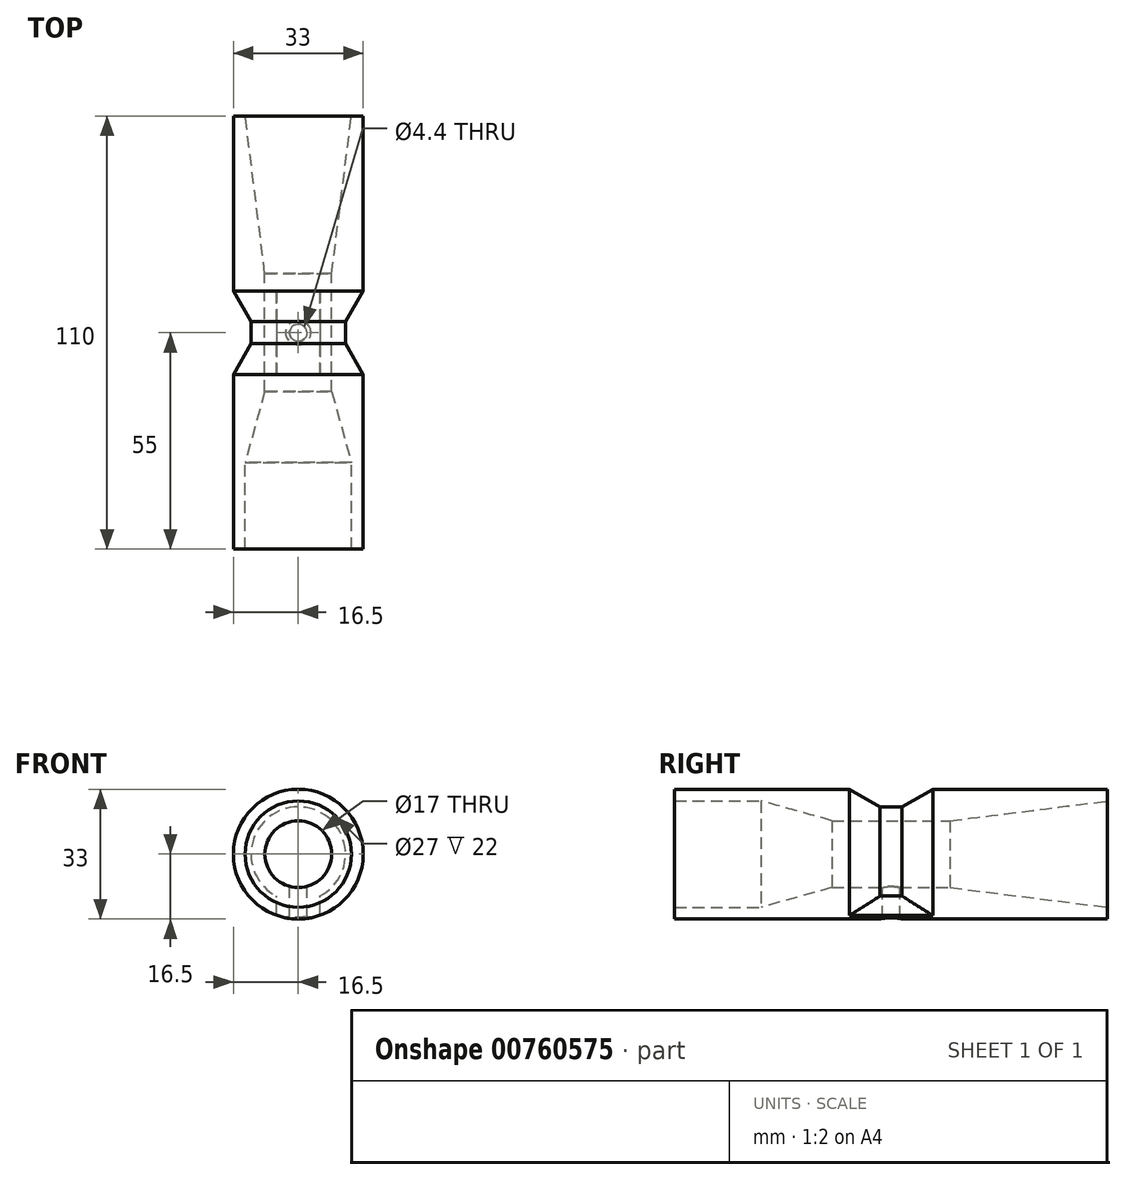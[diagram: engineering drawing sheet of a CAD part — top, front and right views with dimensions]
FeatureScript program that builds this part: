
annotation { "Feature Type Name" : "Feature", "Feature Type Description" : "" }
export const myFeature = defineFeature(function(context is Context, id is Id, definition is map)
    precondition{}
    {
        {
            var Q0;
            Q0=qCreatedBy(makeId("Front.planeOp"),FACE);
            var sketch = newSketch(context, id + "F0", { "sketchPlane" : qUnion([Q0])});
            skCircle(sketch, "E0", {"center": v(0, 0) * mm, "radius": 13.5 * mm});
            skCircle(sketch, "E1", {"center": v(0, 0) * mm, "radius": 16.5 * mm});
            skCircle(sketch, "E2", {"center": v(0, 0) * mm, "radius": 23.5 * mm});
            skCircle(sketch, "E3", {"center": v(0, 0) * mm, "radius": 26.5 * mm});
            skSolve(sketch);
        }
        {
            var Q0;
            Q0=qCreatedBy(makeId("Right.planeOp"),FACE);
            var sketch = newSketch(context, id + "F1", { "sketchPlane" : qUnion([Q0])});
            skLineSegment(sketch, "E4", {"start": v(0, 0) * mm, "end": v(0, 57.21) * mm, "construction": true});
            skLineSegment(sketch, "E5", {"start": v(15, 32.18) * mm, "end": v(15, -25.03) * mm, "construction": true});
            skLineSegment(sketch, "E6", {"start": v(55, 32.18) * mm, "end": v(55, -25.03) * mm, "construction": true});
            skLineSegment(sketch, "E7", {"start": v(55, 13.5) * mm, "end": v(-55, 13.5) * mm});
            skLineSegment(sketch, "E8", {"start": v(-15, 31.27) * mm, "end": v(-15, -25.94) * mm, "construction": true});
            skLineSegment(sketch, "E9", {"start": v(-55, 31.87) * mm, "end": v(-55, -25.34) * mm, "construction": true});
            skPoint(sketch, "E10", {"position": v(-33, 13.5) * mm});
            skLineSegment(sketch, "E11", {"start": v(-15, 8.5) * mm, "end": v(15, 8.5) * mm});
            skLineSegment(sketch, "E12", {"start": v(-15, 8.5) * mm, "end": v(-33, 13.5) * mm});
            skLineSegment(sketch, "E13", {"start": v(15, 8.5) * mm, "end": v(55, 13.5) * mm});
            skLineSegment(sketch, "E14", {"start": v(-32.07, 13.24) * mm, "end": v(-32.07, 0) * mm});
            skLineSegment(sketch, "E15", {"start": v(-32.07, 0) * mm, "end": v(48.4, 0) * mm});
            skLineSegment(sketch, "E16", {"start": v(48.4, 0) * mm, "end": v(48.4, 12.68) * mm});
            skLineSegment(sketch, "E17.MirrorCS", {"start": v(-15, -8.5) * mm, "end": v(15, -8.5) * mm, "construction": true});
            skLineSegment(sketch, "E18.MirrorCS", {"start": v(55, -13.5) * mm, "end": v(-55, -13.5) * mm, "construction": true});
            skLineSegment(sketch, "E19.bottom", {"start": v(10.63, -16.5) * mm, "end": v(-10.62, -16.5) * mm});
            skLineSegment(sketch, "E19.top", {"start": v(10.63, -7.75) * mm, "end": v(-10.62, -7.75) * mm});
            skLineSegment(sketch, "E19.left", {"start": v(10.63, -16.5) * mm, "end": v(10.63, -7.75) * mm});
            skLineSegment(sketch, "E19.right", {"start": v(-10.62, -16.5) * mm, "end": v(-10.62, -7.75) * mm});
            skPoint(sketch, "E19.middle", {"position": v(0, -12.13) * mm});
            skLineSegment(sketch, "E20", {"start": v(0, 0) * mm, "end": v(0, -13.5) * mm, "construction": true});
            skSolve(sketch);
        }
        {
            var Q0;
            Q0=makeQuery(id+"F0.imprint","IMPRINT",FACE,{"disambiguationData":[TD([[makeQuery(id+"F0.imprint","IMPRINT",EDGE,{"derivedFrom":sQuery(id+"F0.wireOp",EDGE,"E0")}),-1.0]])]});
            var Q1;
            Q1=sQuery(id+"F1.wireOp",VERTEX,"E7.end");
            extrude(context, id + "F2", {"entities" : qUnion([Q0]), "endBound" : BoundingType.UP_TO_VERTEX, "depth" : 60 * mm, "endBoundEntityVertex" : qUnion([Q1]), "offsetDistance" : 25 * mm});
        }
        {
            var Q0;
            Q0=makeQuery(id+"F2.opExtrude","CAP_FACE",FACE,{"disambiguationData":[OSD([sQuery(id+"F0.wireOp",EDGE,"E0"),sQuery(id+"F0.wireOp",EDGE,"E1")])],"isStart":true});
            var Q1;
            Q1=sQuery(id+"F1.wireOp",VERTEX,"E7.start");
            extrude(context, id + "F3", {"entities" : qUnion([Q0]), "operationType" : NewBodyOperationType.ADD, "endBound" : BoundingType.UP_TO_VERTEX, "depth" : 25 * mm, "endBoundEntityVertex" : qUnion([Q1]), "offsetDistance" : 25 * mm});
        }
        {
            var Q0;
            Q0=makeQuery(id+"F1.imprint","IMPRINT",FACE,{"disambiguationData":[TD([[makeQuery(id+"F1.imprint","IMPRINT",EDGE,{"derivedFrom":sQuery(id+"F1.wireOp",EDGE,"E11")}),1.0]])]});
            var Q1;
            {var subQ0=sQuery(id+"F0.wireOp",EDGE,"E0");Q1=makeQuery(id+"F3.boolean.opBoolean","MERGE",FACE,{"derivedFrom":[makeQuery(id+"F2.opExtrude","SWEPT_FACE",FACE,{"disambiguationData":[OSD([subQ0])]}),makeQuery(id+"F3.opExtrude","SWEPT_FACE",FACE,{"disambiguationData":[OSD([subQ0])]})]});}
            revolve(context, id + "F4", {"operationType" : NewBodyOperationType.ADD, "entities" : qUnion([Q0]), "axis" : qUnion([Q1]), "revolveType" : RevolveType.FULL});
        }
        {
            var Q0;
            Q0=qCreatedBy(makeId("Front.planeOp"),FACE);
            var Q1;
            Q1=sQuery(id+"F1.wireOp",VERTEX,"E11.start");
            cPlane(context, id + "F5", {"entities" : qUnion([Q0, Q1]), "cplaneType" : CPlaneType.PLANE_POINT, "offset" : 18 * mm, "width" : 150 * mm, "height" : 150 * mm});
        }
        {
            var Q0;
            Q0=qCreatedBy(makeId("Front.planeOp"),FACE);
            var Q1;
            Q1=sQuery(id+"F1.wireOp",VERTEX,"E11.end");
            cPlane(context, id + "F6", {"entities" : qUnion([Q0, Q1]), "cplaneType" : CPlaneType.PLANE_POINT, "offset" : 25 * mm, "width" : 150 * mm, "height" : 150 * mm});
        }
        {
            var Q0;
            Q0=qCreatedBy(makeId("Front.planeOp"),FACE);
            var sketch = newSketch(context, id + "F7", { "sketchPlane" : qUnion([Q0])});
            skCircle(sketch, "E21", {"center": v(0, 0) * mm, "radius": 12 * mm});
            skCircle(sketch, "E22", {"center": v(0, 0) * mm, "radius": 17.5 * mm});
            skSolve(sketch);
        }
        {
            var Q0;
            Q0=makeQuery(id+"F7.imprint","IMPRINT",FACE,{"disambiguationData":[TD([[makeQuery(id+"F7.imprint","IMPRINT",EDGE,{"derivedFrom":sQuery(id+"F7.wireOp",EDGE,"E21")}),-1.0]])]});
            extrude(context, id + "F8", {"entities" : qUnion([Q0]), "operationType" : NewBodyOperationType.REMOVE, "endBound" : BoundingType.SYMMETRIC, "oppositeDirection" : true, "depth" : 21.2 * mm, "offsetDistance" : 25 * mm});
        }
        {
            var Q0;
            Q0=qCreatedBy(makeId("Top.planeOp"),FACE);
            var sketch = newSketch(context, id + "F9", { "sketchPlane" : qUnion([Q0])});
            skCircle(sketch, "E23", {"center": v(0, 0) * mm, "radius": 2.2 * mm});
            skCircle(sketch, "E24", {"center": v(0, 0) * mm, "radius": 3.4 * mm});
            skSolve(sketch);
        }
        {
            var Q0;
            Q0=makeQuery(id+"F9.imprint","IMPRINT",FACE,{"disambiguationData":[TD([[makeQuery(id+"F9.imprint","IMPRINT",EDGE,{"derivedFrom":sQuery(id+"F9.wireOp",EDGE,"E23")}),1.0]])]});
            var Q1;
            Q1=sQuery(id+"F9.wireOp",EDGE,"E23");
            extrude(context, id + "F10", {"entities" : qUnion([Q0]), "operationType" : NewBodyOperationType.REMOVE, "surfaceEntities" : qUnion([Q1]), "oppositeDirection" : true, "depth" : 120 * mm, "offsetDistance" : 25 * mm});
        }
        {
            var Q0;
            Q0=makeQuery(id+"F9.imprint","IMPRINT",FACE,{"disambiguationData":[TD([[makeQuery(id+"F9.imprint","IMPRINT",EDGE,{"derivedFrom":sQuery(id+"F9.wireOp",EDGE,"E23")}),-1.0]])]});
            extrude(context, id + "F11", {"entities" : qUnion([Q0]), "operationType" : NewBodyOperationType.ADD, "oppositeDirection" : true, "depth" : 21.4 * mm, "offsetDistance" : 25 * mm});
        }
        {
            var Q0;
            Q0=makeQuery(id+"F11.boolean.opBoolean","INTERSECT",EDGE,{"derivedFrom":[makeQuery(id+"F8.boolean.opBoolean","COPY",FACE,{"derivedFrom":makeQuery(id+"F8.opExtrude","SWEPT_FACE",FACE,{"disambiguationData":[OSD([sQuery(id+"F7.wireOp",EDGE,"E21")])]})}),makeQuery(id+"F11.opExtrude","SWEPT_FACE",FACE,{"disambiguationData":[OSD([sQuery(id+"F9.wireOp",EDGE,"E24")])]})]});
            fillet(context, id + "F12", {"entities" : qUnion([Q0]), "radius" : 2 * mm, "tangentPropagation" : true, "allowEdgeOverflow" : false});
        }
        {
            var Q0;
            Q0=makeQuery(id+"F11.opExtrude","CAP_FACE",FACE,{"disambiguationData":[OSD([sQuery(id+"F9.wireOp",EDGE,"E23"),sQuery(id+"F9.wireOp",EDGE,"E24")])],"isStart":false});
            var sketch = newSketch(context, id + "F13", { "sketchPlane" : qUnion([Q0])});
            skCircle(sketch, "E25", {"center": v(0, 0) * mm, "radius": 5.5 * mm});
            skSolve(sketch);
        }
        {
            var Q0;
            Q0=makeQuery(id+"F13.imprint","IMPRINT",FACE,{"disambiguationData":[TD([[makeQuery(id+"F13.imprint","IMPRINT",EDGE,{"derivedFrom":sQuery(id+"F13.wireOp",EDGE,"E25")}),1.0]])]});
            extrude(context, id + "F14", {"entities" : qUnion([Q0]), "operationType" : NewBodyOperationType.ADD, "endBound" : BoundingType.UP_TO_NEXT, "oppositeDirection" : true, "depth" : 25 * mm, "offsetDistance" : 25 * mm});
        }
        {
            var Q0;
            Q0=makeQuery(id+"F8.boolean.opBoolean","COPY",EDGE,{"derivedFrom":makeQuery(id+"F8.opExtrude","CAP_EDGE",EDGE,{"disambiguationData":[OSD([sQuery(id+"F7.wireOp",EDGE,"E21")])],"isStart":true})});
            var Q1;
            Q1=makeQuery(id+"F8.boolean.opBoolean","COPY",EDGE,{"derivedFrom":makeQuery(id+"F8.opExtrude","CAP_EDGE",EDGE,{"disambiguationData":[OSD([sQuery(id+"F7.wireOp",EDGE,"E21")])],"isStart":false})});
            chamfer(context, id + "F15", {"entities" : qUnion([Q0, Q1]), "chamferType" : ChamferType.OFFSET_ANGLE, "width" : 4.5 * mm, "oppositeDirection" : false, "angle" : 60 * degree, "tangentPropagation" : true});
        }
        {
            var Q0;
            {var subQ0=sQuery(id+"F9.wireOp",EDGE,"E24");Q0=makeQuery(id+"F14.boolean.opBoolean","MERGE",FACE,{"derivedFrom":[makeQuery(id+"F11.opExtrude","CAP_FACE",FACE,{"disambiguationData":[OSD([sQuery(id+"F9.wireOp",EDGE,"E23"),subQ0])],"isStart":false}),makeQuery(id+"F14.opExtrude","CAP_FACE",FACE,{"disambiguationData":[OSD([subQ0,sQuery(id+"F13.wireOp",EDGE,"E25")])],"isStart":true})]});}
            extrude(context, id + "F16", {"entities" : qUnion([Q0]), "operationType" : NewBodyOperationType.REMOVE, "oppositeDirection" : true, "depth" : 4.85 * mm, "offsetDistance" : 25 * mm});
        }
        {
            var Q0;
            Q0=makeQuery(id+"F1.imprint","IMPRINT",FACE,{"disambiguationData":[TD([[makeQuery(id+"F1.imprint","IMPRINT",EDGE,{"derivedFrom":sQuery(id+"F1.wireOp",EDGE,"E19.bottom")}),-1.0]])]});
            extrude(context, id + "F17", {"entities" : qUnion([Q0]), "operationType" : NewBodyOperationType.ADD, "endBound" : BoundingType.SYMMETRIC, "depth" : 11.04 * mm, "offsetDistance" : 25 * mm});
        }
        {
            var Q0;
            Q0=makeQuery(id+"F2.opExtrude","CAP_FACE",FACE,{"disambiguationData":[OSD([sQuery(id+"F0.wireOp",EDGE,"E0"),sQuery(id+"F0.wireOp",EDGE,"E1")])],"isStart":false});
            var sketch = newSketch(context, id + "F18", { "sketchPlane" : qUnion([Q0])});
            skCircle(sketch, "E26", {"center": v(0, 0) * mm, "radius": 26.69 * mm});
            skSolve(sketch);
        }
        {
            var Q0;
            Q0=makeQuery(id+"F18.imprint","IMPRINT",FACE,{"disambiguationData":[TD([[makeQuery(id+"F18.imprint","IMPRINT",EDGE,{"derivedFrom":sQuery(id+"F18.wireOp",EDGE,"E26")}),1.0]])]});
            var Q1;
            Q1=makeQuery(id+"F3.opExtrude","CAP_FACE",FACE,{"disambiguationData":[OSD([sQuery(id+"F0.wireOp",EDGE,"E0"),sQuery(id+"F0.wireOp",EDGE,"E1")])],"isStart":false});
            extrude(context, id + "F19", {"entities" : qUnion([Q0]), "operationType" : NewBodyOperationType.REMOVE, "endBound" : BoundingType.UP_TO_SURFACE, "oppositeDirection" : true, "depth" : 25 * mm, "endBoundEntityFace" : qUnion([Q1]), "offsetDistance" : 25 * mm});
        }
        {
            var Q0;
            {var subQ1=sQuery(id+"F1.wireOp",EDGE,"E11");Q0=makeQuery(id+"F1.imprint","IMPRINT",FACE,{"disambiguationData":[TD([[makeQuery(id+"F1.imprint","IMPRINT",EDGE,{"derivedFrom":subQ1}),-1.0]])]});}
            var Q1;
            Q1=makeQuery(id+"F4.opRevolve","SWEPT_FACE",FACE,{"disambiguationData":[OSD([sQuery(id+"F1.wireOp",EDGE,"E11")])]});
            revolve(context, id + "F20", {"operationType" : NewBodyOperationType.REMOVE, "surfaceOperationType" : NewSurfaceOperationType.NEW, "entities" : qUnion([Q0]), "axis" : qUnion([Q1]), "revolveType" : RevolveType.FULL, "oppositeDirection" : true});
        }
        {
            var Q0;
            Q0=makeQuery(id+"F9.imprint","IMPRINT",FACE,{"disambiguationData":[TD([[makeQuery(id+"F9.imprint","IMPRINT",EDGE,{"derivedFrom":sQuery(id+"F9.wireOp",EDGE,"E23")}),1.0]])]});
            extrude(context, id + "F21", {"entities" : qUnion([Q0]), "operationType" : NewBodyOperationType.REMOVE, "oppositeDirection" : true, "depth" : 25 * mm, "offsetDistance" : 25 * mm});
        }
        {
            var Q0;
            {var subQ0=sQuery(id+"F0.wireOp",EDGE,"E1");var subQ1=sQuery(id+"F0.wireOp",EDGE,"E0");var subQ4=makeQuery(id+"F3.boolean.opBoolean","MERGE",FACE,{"derivedFrom":[makeQuery(id+"F2.opExtrude","SWEPT_FACE",FACE,{"disambiguationData":[OSD([subQ0])]}),makeQuery(id+"F3.opExtrude","SWEPT_FACE",FACE,{"disambiguationData":[OSD([subQ0])]})]});Q0=makeQuery(id+"F21.boolean.opBoolean","INTERSECT",EDGE,{"derivedFrom":[makeQuery(id+"F19.boolean.opBoolean","MERGE",FACE,{"derivedFrom":[makeQuery(id+"F8.boolean.opBoolean","SPLIT",FACE,{"disambiguationData":[TD([makeQuery(id+"F2.opExtrude","CAP_FACE",FACE,{"disambiguationData":[OSD([subQ1,subQ0])],"isStart":false})])],"derivedFrom":subQ4}),makeQuery(id+"F8.boolean.opBoolean","SPLIT",FACE,{"disambiguationData":[TD([makeQuery(id+"F3.opExtrude","CAP_FACE",FACE,{"disambiguationData":[OSD([subQ1,subQ0])],"isStart":false})])],"derivedFrom":subQ4})],"fromTools":[makeQuery(id+"F19.opExtrude","SWEPT_FACE",FACE,{"disambiguationData":[OSD([subQ0])]})]}),makeQuery(id+"F21.opExtrude","SWEPT_FACE",FACE,{"disambiguationData":[OSD([sQuery(id+"F9.wireOp",EDGE,"E23")])]})]});}
            chamfer(context, id + "F22", {"entities" : qUnion([Q0]), "chamferType" : ChamferType.OFFSET_ANGLE, "width" : 1 * mm, "oppositeDirection" : false, "angle" : 30 * degree, "tangentPropagation" : true});
        }
    });
